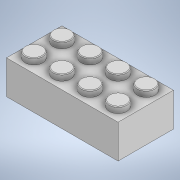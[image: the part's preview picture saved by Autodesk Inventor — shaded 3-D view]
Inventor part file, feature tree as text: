
AUTODESK INVENTOR PART (.ipt)
format: ipt  version: 2020 (Build 240168000, 168)  size: 227,840 bytes
history: native  units: mm
features: extrude x3, sketch x3, pattern_linear x2, shell x1, plane x1, fillet x1
ambient origin geometry x8: Origin, YZ Plane, XZ Plane, XY Plane, X Axis, Y Axis, Z Axis, Center Point
bodies: Solid1 (feature_tree)
feature tree (11):
  extrude  "Extrusion1"  Depth=15.8mm
  extrude  "Extrusion2"  Depth=9.6mm
  pattern_linear  "Rectangular Pattern1"  Spacing1=3.9mm  [1 undecoded]
  shell  "Shell1"  Thickness=1.7mm
  plane  "Work Plane1"
  extrude  "Extrusion3"  Depth=0.2mm
  pattern_linear  "Rectangular Pattern2"  Spacing1=1.49mm  [1 undecoded]
  fillet  "Fillet1"  Radius=9.0mm
  sketch  "Sketch1"  dims[d0=31.8mm d1=15.8mm]
  sketch  "Sketch3"  dims[d2=9.6mm d3=0.0mm d4=5.0mm]
  sketch  "Sketch4"  dims[d5=3.9mm d6=3.9mm d7=1.7mm d8=0.0mm d9=20.0mm d11=8.0mm d12=40.0mm d14=24.0mm d15=1.49mm d16=9.0mm d17=4.314mm d18=8.1mm d19=0.0mm d20=30.0mm d22=16.0mm d23=0.2mm d21=0.872665mm]
note: 2 required parameter values undecoded (feature->parameter linkage not recoverable at this tier; creation-order binding heuristic only, values carry confidence <= 0.55)
